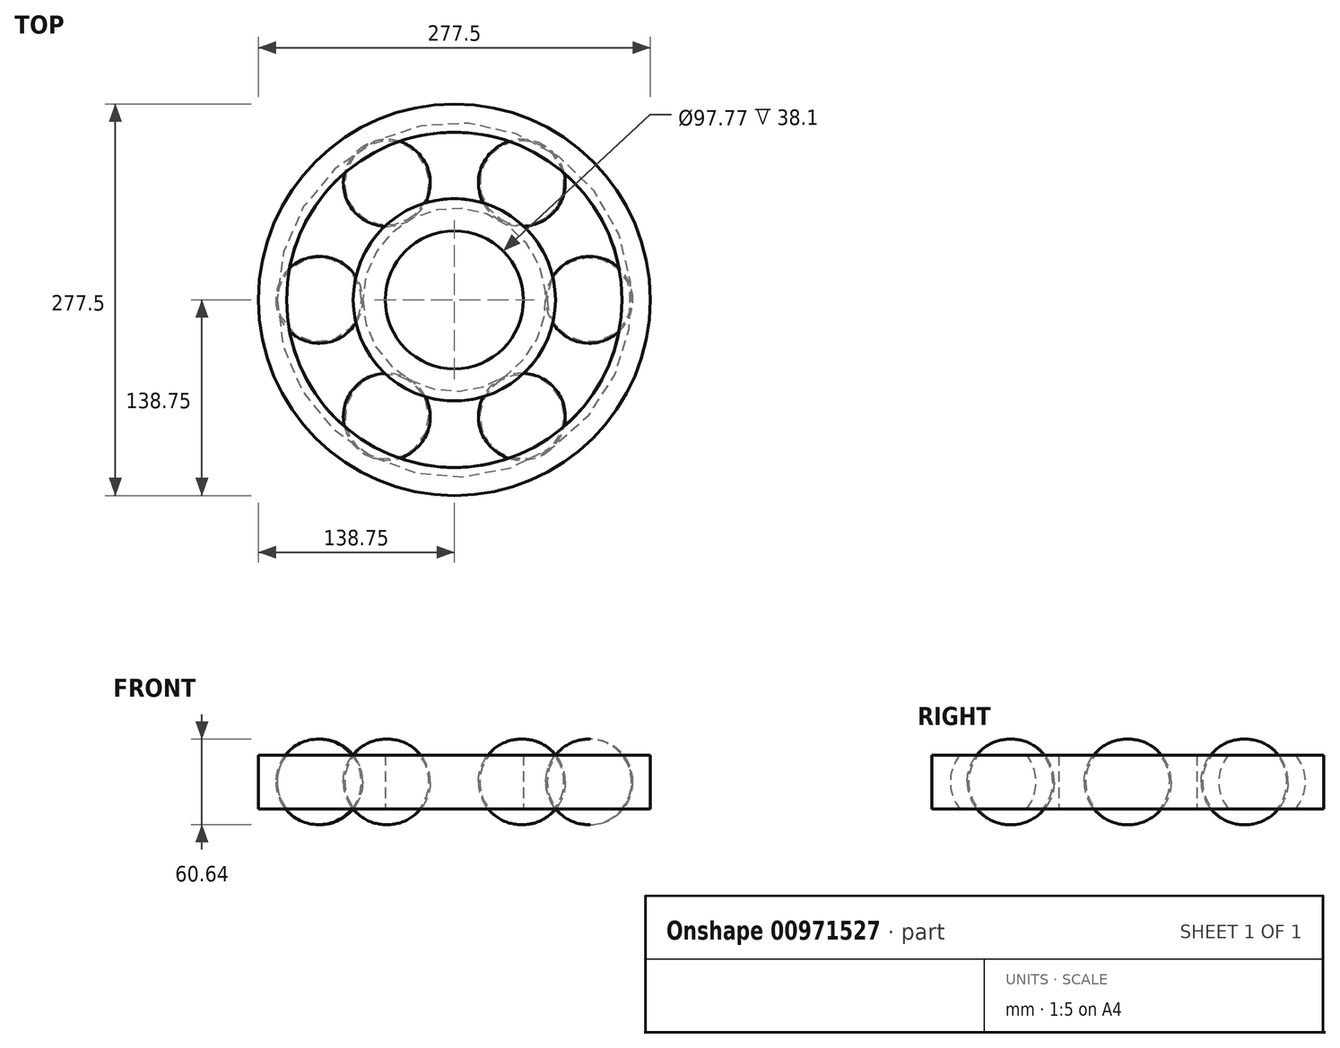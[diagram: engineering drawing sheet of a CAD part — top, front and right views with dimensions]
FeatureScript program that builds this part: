
annotation { "Feature Type Name" : "Feature", "Feature Type Description" : "" }
export const myFeature = defineFeature(function(context is Context, id is Id, definition is map)
    precondition{}
    {
        {
            var Q0;
            Q0=qCreatedBy(makeId("Front.planeOp"),FACE);
            var sketch = newSketch(context, id + "F0", { "sketchPlane" : qUnion([Q0])});
            skLineSegment(sketch, "E0", {"start": v(0, 0) * mm, "end": v(0, 67.6) * mm, "construction": true});
            skLineSegment(sketch, "E1.bottom", {"start": v(48.89, 19.05) * mm, "end": v(76.77, 19.05) * mm});
            skLineSegment(sketch, "E1.top", {"start": v(48.89, -19.05) * mm, "end": v(76.77, -19.05) * mm});
            skLineSegment(sketch, "E1.left", {"start": v(48.89, 19.05) * mm, "end": v(48.89, -19.05) * mm});
            skLineSegment(sketch, "E1.right", {"start": v(76.77, 19.05) * mm, "end": v(76.77, -19.05) * mm});
            skPoint(sketch, "E1.middle", {"position": v(62.83, 0) * mm});
            skCircle(sketch, "E2", {"center": v(95.2, 0) * mm, "radius": 30.32 * mm});
            skLineSegment(sketch, "E3.1.0.0", {"start": v(110.86, 19.05) * mm, "end": v(110.86, -19.05) * mm});
            skLineSegment(sketch, "E3.1.0.1", {"start": v(110.86, 19.05) * mm, "end": v(138.75, 19.05) * mm});
            skLineSegment(sketch, "E3.1.0.2", {"start": v(138.75, 19.05) * mm, "end": v(138.75, -19.05) * mm});
            skLineSegment(sketch, "E3.1.0.3", {"start": v(110.86, -19.05) * mm, "end": v(138.75, -19.05) * mm});
            skLineSegment(sketch, "E3.direction1", {"start": v(48.89, -19.05) * mm, "end": v(110.86, -19.05) * mm, "construction": true});
            skLineSegment(sketch, "E4", {"start": v(48.89, 0) * mm, "end": v(138.75, 0) * mm, "construction": true});
            skLineSegment(sketch, "E5", {"start": v(95.65, 30.31) * mm, "end": v(95.65, -30.31) * mm});
            skSolve(sketch);
        }
        {
            var Q0;
            {var subQ1=sQuery(id+"F0.wireOp",EDGE,"E3.1.0.0");Q0=makeQuery(id+"F0.imprint","IMPRINT",FACE,{"disambiguationData":[TD([[makeQuery(id+"F0.imprint","IMPRINT",EDGE,{"derivedFrom":subQ1}),-1.0]])]});}
            var Q1;
            {var subQ5=sQuery(id+"F0.wireOp",EDGE,"E3.1.0.0");Q1=makeQuery(id+"F0.imprint","IMPRINT",FACE,{"disambiguationData":[TD([[makeQuery(id+"F0.imprint","IMPRINT",EDGE,{"derivedFrom":subQ5}),1.0]])]});}
            var Q2;
            Q2=sQuery(id+"F0.wireOp",EDGE,"E5");
            revolve(context, id + "F1", {"surfaceOperationType" : NewSurfaceOperationType.NEW, "entities" : qUnion([Q0, Q1]), "axis" : qUnion([Q2]), "revolveType" : RevolveType.FULL});
        }
        {
            var Q0;
            {var subQ5=sQuery(id+"F0.wireOp",EDGE,"E3.1.0.2");Q0=makeQuery(id+"F0.imprint","IMPRINT",FACE,{"disambiguationData":[TD([[makeQuery(id+"F0.imprint","IMPRINT",EDGE,{"derivedFrom":subQ5}),-1.0]])]});}
            var Q1;
            {var subQ0=sQuery(id+"F0.wireOp",EDGE,"E1.left");Q1=makeQuery(id+"F0.imprint","IMPRINT",FACE,{"disambiguationData":[TD([[makeQuery(id+"F0.imprint","IMPRINT",EDGE,{"derivedFrom":subQ0}),1.0]])]});}
            var Q2;
            Q2=sQuery(id+"F0.wireOp",EDGE,"E0");
            revolve(context, id + "F2", {"surfaceOperationType" : NewSurfaceOperationType.NEW, "entities" : qUnion([Q0, Q1]), "axis" : qUnion([Q2]), "revolveType" : RevolveType.FULL});
        }
        {
            var Q0;
            Q0=makeQuery(id+"F1.opRevolve","SWEPT_BODY",BODY,{"disambiguationData":[OSD([sQuery(id+"F0.wireOp",EDGE,"E2"),sQuery(id+"F0.wireOp",EDGE,"E5")])]});
            var Q1;
            Q1=sQuery(id+"F0.wireOp",EDGE,"E0");
            circularPattern(context, id + "F3", {"entities" : qUnion([Q0]), "axis" : qUnion([Q1]), "angle" : 360 * degree, "instanceCount" : 6, "equalSpace" : true});
        }
    });
